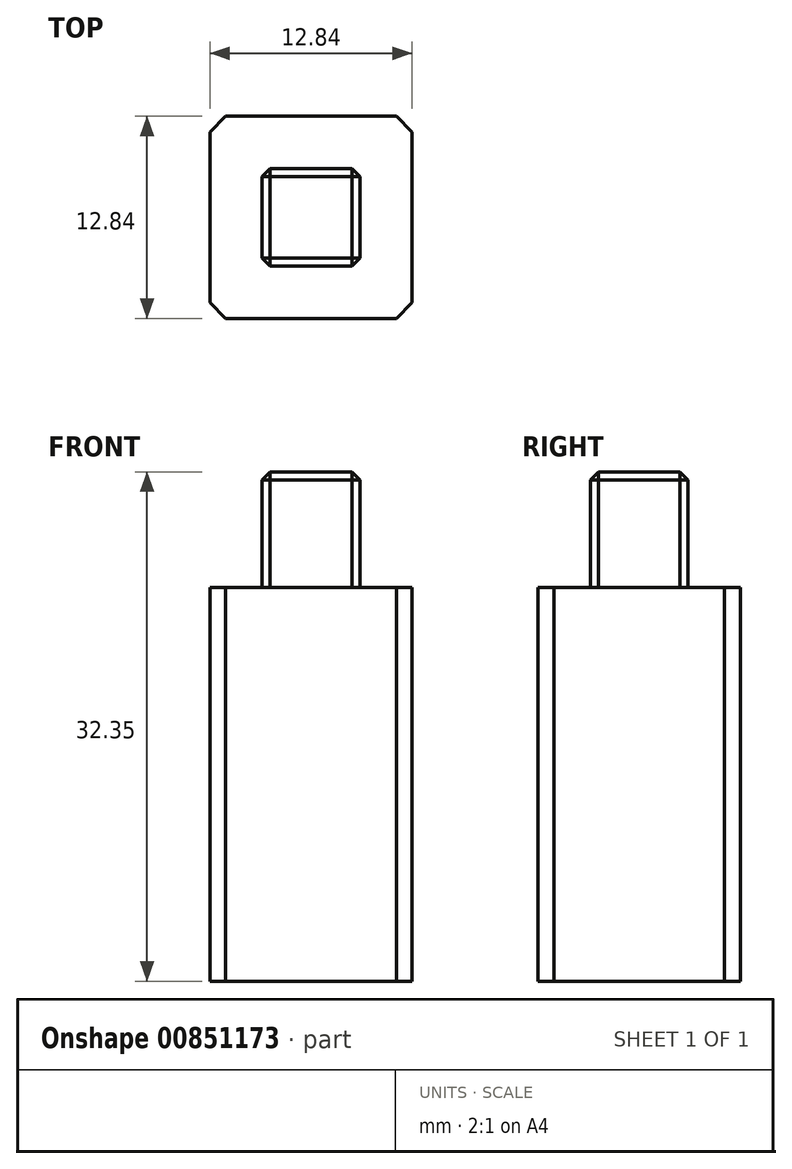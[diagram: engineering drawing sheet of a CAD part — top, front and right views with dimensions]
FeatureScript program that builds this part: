
annotation { "Feature Type Name" : "Feature", "Feature Type Description" : "" }
export const myFeature = defineFeature(function(context is Context, id is Id, definition is map)
    precondition{}
    {
        {
            var Q0;
            Q0=qCreatedBy(makeId("Top.planeOp"),FACE);
            var sketch = newSketch(context, id + "F0", { "sketchPlane" : qUnion([Q0])});
            skLineSegment(sketch, "E0.bottom", {"start": v(6.42, -6.43) * mm, "end": v(-6.42, -6.43) * mm});
            skLineSegment(sketch, "E0.top", {"start": v(6.42, 6.42) * mm, "end": v(-6.42, 6.42) * mm});
            skLineSegment(sketch, "E0.left", {"start": v(6.42, -6.43) * mm, "end": v(6.42, 6.42) * mm});
            skLineSegment(sketch, "E0.right", {"start": v(-6.42, -6.43) * mm, "end": v(-6.42, 6.42) * mm});
            skPoint(sketch, "E0.middle", {"position": v(0, 0) * mm});
            skLineSegment(sketch, "E1.bottom", {"start": v(3.1, -3.1) * mm, "end": v(-3.1, -3.1) * mm});
            skLineSegment(sketch, "E1.top", {"start": v(3.1, 3.1) * mm, "end": v(-3.1, 3.1) * mm});
            skLineSegment(sketch, "E1.left", {"start": v(3.1, -3.1) * mm, "end": v(3.1, 3.1) * mm});
            skLineSegment(sketch, "E1.right", {"start": v(-3.1, -3.1) * mm, "end": v(-3.1, 3.1) * mm});
            skSolve(sketch);
        }
        {
            var Q0;
            Q0=makeQuery(id+"F0.imprint","IMPRINT",FACE,{"disambiguationData":[TD([[makeQuery(id+"F0.imprint","IMPRINT",EDGE,{"derivedFrom":sQuery(id+"F0.wireOp",EDGE,"E0.bottom")}),-1.0]])]});
            extrude(context, id + "F1", {"entities" : qUnion([Q0]), "depth" : 25 * mm, "offsetDistance" : 25 * mm});
        }
        {
            var Q0;
            Q0=makeQuery(id+"F0.imprint","IMPRINT",FACE,{"disambiguationData":[TD([[makeQuery(id+"F0.imprint","IMPRINT",EDGE,{"derivedFrom":sQuery(id+"F0.wireOp",EDGE,"E1.bottom")}),-1.0]])]});
            extrude(context, id + "F2", {"entities" : qUnion([Q0]), "operationType" : NewBodyOperationType.ADD, "depth" : 32.35 * mm, "offsetDistance" : 25 * mm});
        }
        {
            var Q0;
            Q0=makeQuery(id+"F2.opExtrude","SWEPT_EDGE",EDGE,{"disambiguationData":[OSD([sQuery(id+"F0.wireOp",EDGE,"E1.bottom"),sQuery(id+"F0.wireOp",EDGE,"E1.left")])]});
            var Q1;
            Q1=makeQuery(id+"F2.opExtrude","SWEPT_EDGE",EDGE,{"disambiguationData":[OSD([sQuery(id+"F0.wireOp",EDGE,"E1.top"),sQuery(id+"F0.wireOp",EDGE,"E1.left")])]});
            var Q2;
            Q2=makeQuery(id+"F2.opExtrude","SWEPT_EDGE",EDGE,{"disambiguationData":[OSD([sQuery(id+"F0.wireOp",EDGE,"E1.bottom"),sQuery(id+"F0.wireOp",EDGE,"E1.right")])]});
            var Q3;
            Q3=makeQuery(id+"F2.opExtrude","SWEPT_EDGE",EDGE,{"disambiguationData":[OSD([sQuery(id+"F0.wireOp",EDGE,"E1.top"),sQuery(id+"F0.wireOp",EDGE,"E1.right")])]});
            var Q4;
            Q4=makeQuery(id+"F2.opExtrude","CAP_EDGE",EDGE,{"disambiguationData":[OSD([sQuery(id+"F0.wireOp",EDGE,"E1.right")])],"isStart":false});
            var Q5;
            Q5=makeQuery(id+"F2.opExtrude","CAP_EDGE",EDGE,{"disambiguationData":[OSD([sQuery(id+"F0.wireOp",EDGE,"E1.top")])],"isStart":false});
            var Q6;
            Q6=makeQuery(id+"F2.opExtrude","CAP_EDGE",EDGE,{"disambiguationData":[OSD([sQuery(id+"F0.wireOp",EDGE,"E1.left")])],"isStart":false});
            var Q7;
            Q7=makeQuery(id+"F2.opExtrude","CAP_EDGE",EDGE,{"disambiguationData":[OSD([sQuery(id+"F0.wireOp",EDGE,"E1.bottom")])],"isStart":false});
            chamfer(context, id + "F3", {"entities" : qUnion([Q0, Q1, Q2, Q3, Q4, Q5, Q6, Q7]), "width" : .5 * mm, "tangentPropagation" : true});
        }
        {
            var Q0;
            Q0=makeQuery(id+"F1.opExtrude","SWEPT_EDGE",EDGE,{"disambiguationData":[OSD([sQuery(id+"F0.wireOp",EDGE,"E0.bottom"),sQuery(id+"F0.wireOp",EDGE,"E0.right")])]});
            var Q1;
            Q1=makeQuery(id+"F1.opExtrude","SWEPT_EDGE",EDGE,{"disambiguationData":[OSD([sQuery(id+"F0.wireOp",EDGE,"E0.top"),sQuery(id+"F0.wireOp",EDGE,"E0.right")])]});
            var Q2;
            Q2=makeQuery(id+"F1.opExtrude","SWEPT_EDGE",EDGE,{"disambiguationData":[OSD([sQuery(id+"F0.wireOp",EDGE,"E0.top"),sQuery(id+"F0.wireOp",EDGE,"E0.left")])]});
            var Q3;
            Q3=makeQuery(id+"F1.opExtrude","SWEPT_EDGE",EDGE,{"disambiguationData":[OSD([sQuery(id+"F0.wireOp",EDGE,"E0.bottom"),sQuery(id+"F0.wireOp",EDGE,"E0.left")])]});
            chamfer(context, id + "F4", {"entities" : qUnion([Q0, Q1, Q2, Q3]), "width" : 1 * mm, "tangentPropagation" : true});
        }
    });
